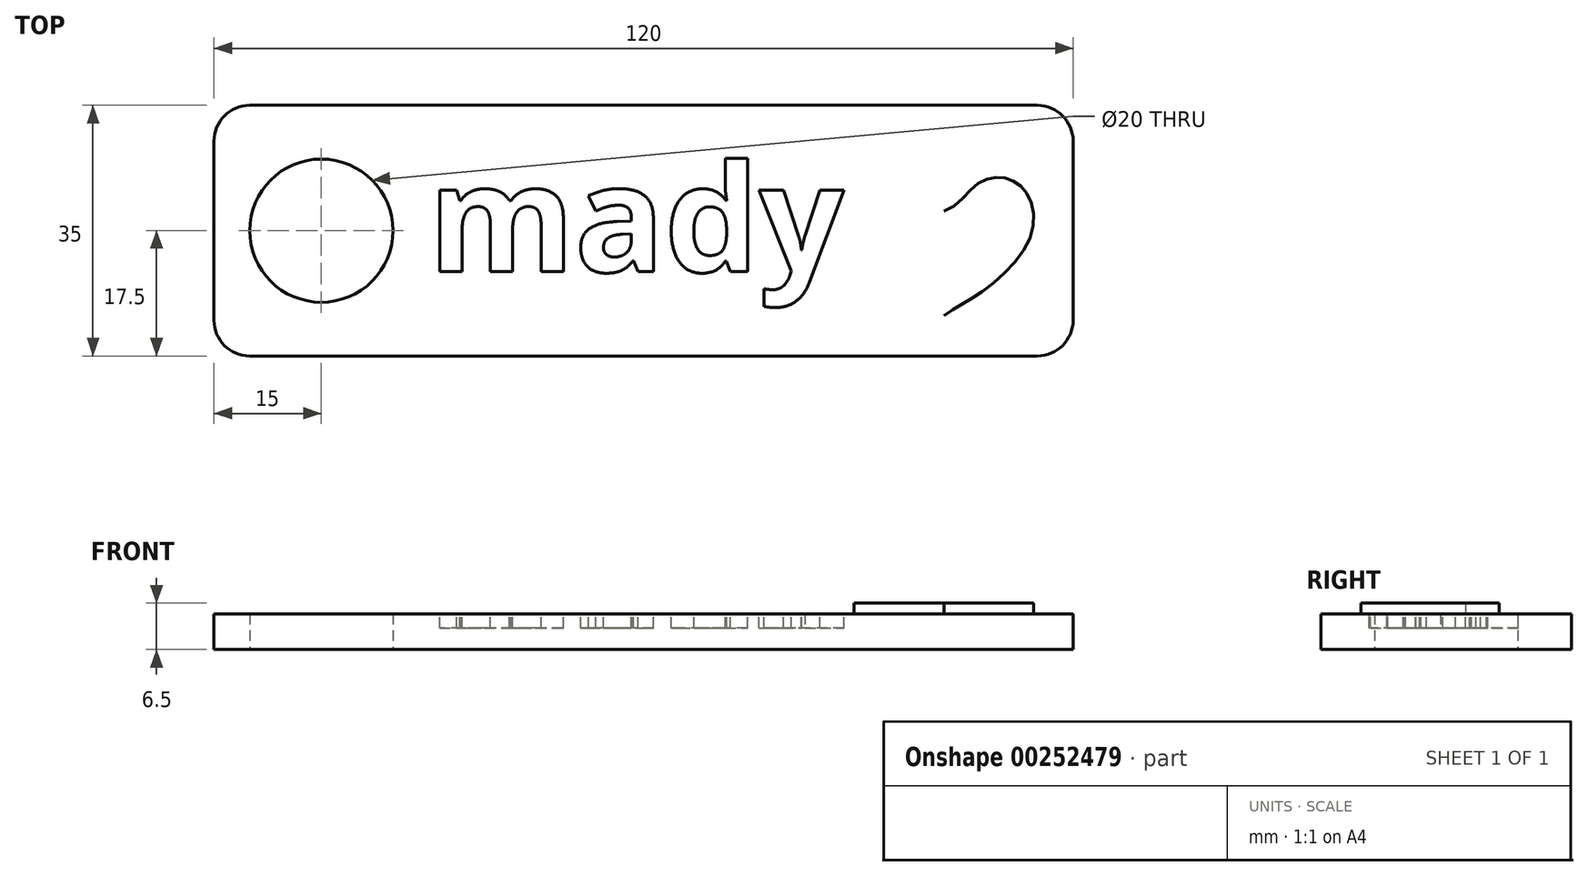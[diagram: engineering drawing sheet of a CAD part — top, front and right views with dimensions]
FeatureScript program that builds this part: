
annotation { "Feature Type Name" : "Feature", "Feature Type Description" : "" }
export const myFeature = defineFeature(function(context is Context, id is Id, definition is map)
    precondition{}
    {
        {
            var Q0;
            Q0=qCreatedBy(makeId("Top.planeOp"),FACE);
            var sketch = newSketch(context, id + "F0", { "sketchPlane" : qUnion([Q0])});
            skLineSegment(sketch, "E0.bottom", {"start": v(-60, -17.5) * mm, "end": v(60, -17.5) * mm});
            skLineSegment(sketch, "E0.top", {"start": v(-60, 17.5) * mm, "end": v(60, 17.5) * mm});
            skLineSegment(sketch, "E0.left", {"start": v(-60, -17.5) * mm, "end": v(-60, 17.5) * mm});
            skLineSegment(sketch, "E0.right", {"start": v(60, -17.5) * mm, "end": v(60, 17.5) * mm});
            skPoint(sketch, "E0.middle", {"position": v(0, 0) * mm});
            skCircle(sketch, "E1", {"center": v(-45, 0) * mm, "radius": 10 * mm});
            skSolve(sketch);
        }
        {
            var Q0;
            Q0=makeQuery(id+"F0.imprint","IMPRINT",FACE,{"disambiguationData":[TD([[makeQuery(id+"F0.imprint","IMPRINT",EDGE,{"derivedFrom":sQuery(id+"F0.wireOp",EDGE,"E0.bottom")}),1.0]])]});
            extrude(context, id + "F1", {"entities" : qUnion([Q0]), "depth" : 5 * mm});
        }
        {
            var Q0;
            Q0=makeQuery(id+"F1.opExtrude","SWEPT_EDGE",EDGE,{"disambiguationData":[OSD([sQuery(id+"F0.wireOp",EDGE,"E0.bottom"),sQuery(id+"F0.wireOp",EDGE,"E0.right")])]});
            var Q1;
            Q1=makeQuery(id+"F1.opExtrude","SWEPT_EDGE",EDGE,{"disambiguationData":[OSD([sQuery(id+"F0.wireOp",EDGE,"E0.top"),sQuery(id+"F0.wireOp",EDGE,"E0.right")])]});
            var Q2;
            Q2=makeQuery(id+"F1.opExtrude","SWEPT_EDGE",EDGE,{"disambiguationData":[OSD([sQuery(id+"F0.wireOp",EDGE,"E0.bottom"),sQuery(id+"F0.wireOp",EDGE,"E0.left")])]});
            var Q3;
            Q3=makeQuery(id+"F1.opExtrude","SWEPT_EDGE",EDGE,{"disambiguationData":[OSD([sQuery(id+"F0.wireOp",EDGE,"E0.top"),sQuery(id+"F0.wireOp",EDGE,"E0.left")])]});
            fillet(context, id + "F2", {"entities" : qUnion([Q0, Q1, Q2, Q3]), "radius" : 5 * mm, "tangentPropagation" : true, "allowEdgeOverflow" : false});
        }
        {
            var Q0;
            Q0=makeQuery(id+"F1.opExtrude","CAP_FACE",FACE,{"disambiguationData":[OSD([sQuery(id+"F0.wireOp",EDGE,"E0.bottom"),sQuery(id+"F0.wireOp",EDGE,"E0.top"),sQuery(id+"F0.wireOp",EDGE,"E0.left"),sQuery(id+"F0.wireOp",EDGE,"E0.right"),sQuery(id+"F0.wireOp",EDGE,"E1")])],"isStart":false});
            var sketch = newSketch(context, id + "F3", { "sketchPlane" : qUnion([Q0])});
            skText(sketch, "E2", { "text": "mady\n", "fontName": "OpenSans-Bold.ttf"});
            const initialGuessF3  = {"E2": [-0.0301, -0.00574, 1, 0, 0.015]};
            skSetInitialGuess(sketch, initialGuessF3);
            skSolve(sketch);
        }
        {
            var Q0;
            Q0 = qSketchRegion(id + "F3", true);
            extrude(context, id + "F4", {"entities" : qUnion([Q0]), "operationType" : NewBodyOperationType.REMOVE, "oppositeDirection" : true, "depth" : 2 * mm});
        }
        {
            var Q0;
            Q0=makeQuery(id+"F3.imprint","IMPRINT",FACE,{"disambiguationData":[TD([[makeQuery(id+"F3.imprint","IMPRINT",EDGE,{"derivedFrom":sQuery(id+"F3.wireOp",EDGE,"E2.sketch_text.stroke-0")}),1.0]])]});
            var sketch = newSketch(context, id + "F5", { "sketchPlane" : qUnion([Q0])});
            skLineSegment(sketch, "E3", {"start": v(41.94, 37.11) * mm, "end": v(41.94, -46.97) * mm, "construction": true});
            skFitSpline(sketch, "E4", {"points": [v(41.94, 2.73) * mm, v(46.56, 6.48) * mm, v(50.46, 7.35) * mm, v(53.64, 5.04) * mm, v(53.93, -1.17) * mm, v(47.23, -8.54) * mm, v(41.94, -11.86) * mm], "startDerivative": vector(36.22, 10.35) * mm, "endDerivative": vector(-27.38, -18.96) * mm});
            skFitSpline(sketch, "E5.MirrorCS", {"points": [v(41.94, 2.73) * mm, v(37.32, 6.48) * mm, v(33.42, 7.35) * mm, v(30.24, 5.04) * mm, v(29.95, -1.17) * mm, v(36.66, -8.54) * mm, v(41.94, -11.86) * mm], "startDerivative": vector(-36.22, 10.35) * mm, "endDerivative": vector(27.38, -18.96) * mm});
            skSolve(sketch);
        }
        {
            var Q0;
            Q0 = qSketchRegion(id + "F5", true);
            extrude(context, id + "F6", {"entities" : qUnion([Q0]), "operationType" : NewBodyOperationType.ADD, "depth" : 1.5 * mm});
        }
    });
